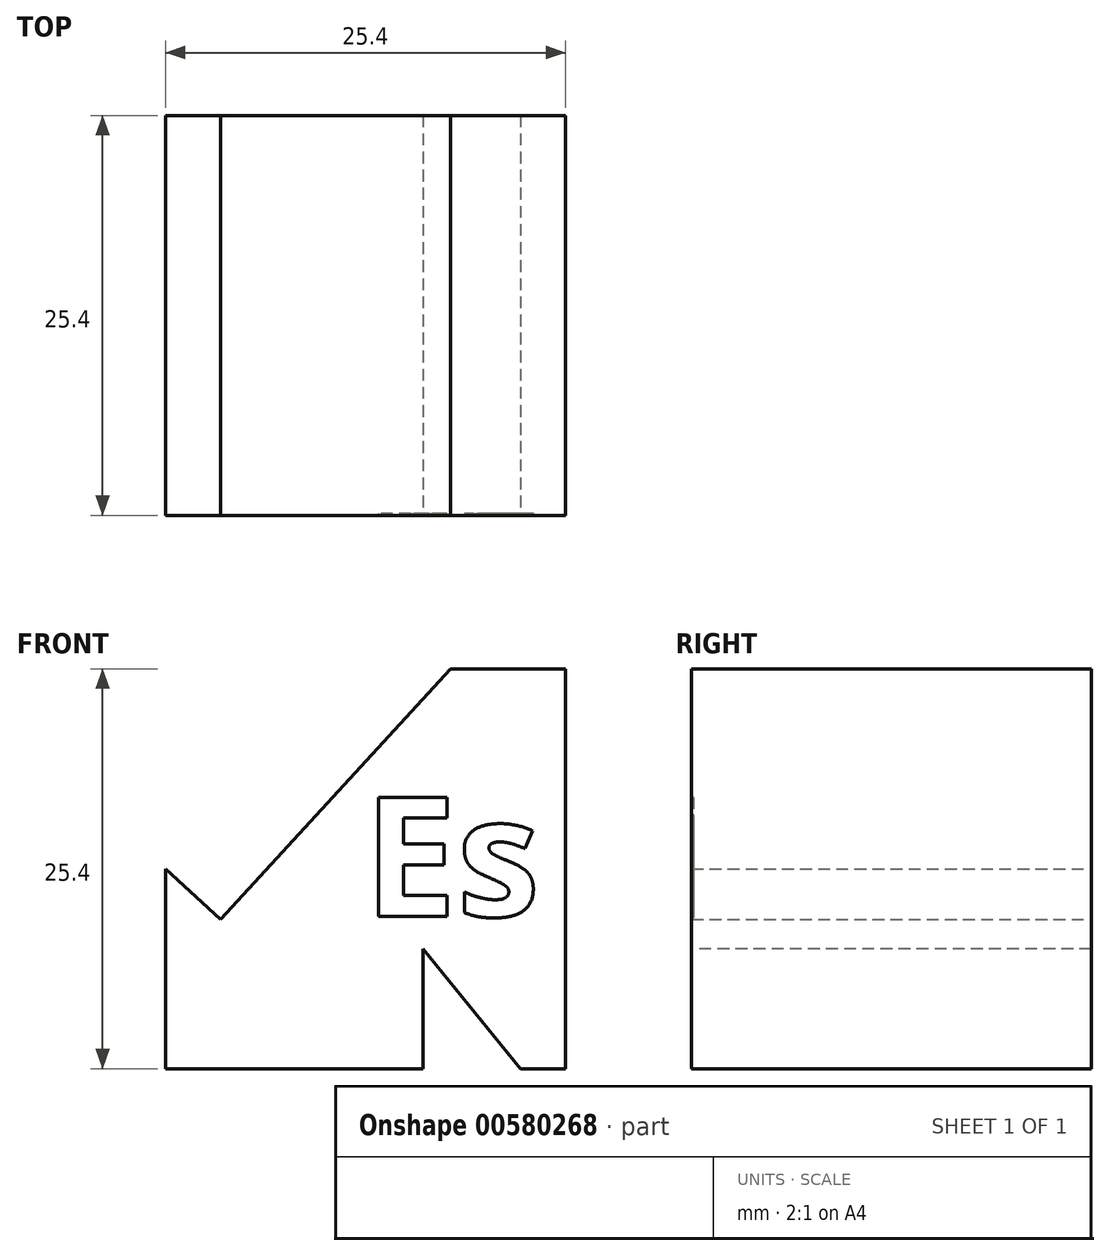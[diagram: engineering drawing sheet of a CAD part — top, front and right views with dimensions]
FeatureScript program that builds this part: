
annotation { "Feature Type Name" : "Feature", "Feature Type Description" : "" }
export const myFeature = defineFeature(function(context is Context, id is Id, definition is map)
    precondition{}
    {
        {
            var Q0;
            Q0=qCreatedBy(makeId("Front.planeOp"),FACE);
            var sketch = newSketch(context, id + "F0", { "sketchPlane" : qUnion([Q0])});
            skLineSegment(sketch, "E0.bottom", {"start": v(-12.7, 12.7) * mm, "end": v(12.7, 12.7) * mm});
            skLineSegment(sketch, "E0.top", {"start": v(-12.7, -12.7) * mm, "end": v(12.7, -12.7) * mm});
            skLineSegment(sketch, "E0.left", {"start": v(-12.7, 12.7) * mm, "end": v(-12.7, -12.7) * mm});
            skLineSegment(sketch, "E0.right", {"start": v(12.7, 12.7) * mm, "end": v(12.7, -12.7) * mm});
            skPoint(sketch, "E0.middle", {"position": v(0, 0) * mm});
            skSolve(sketch);
        }
        {
            var Q0;
            Q0=makeQuery(id+"F0.imprint","IMPRINT",FACE,{"disambiguationData":[TD([[makeQuery(id+"F0.imprint","IMPRINT",EDGE,{"derivedFrom":sQuery(id+"F0.wireOp",EDGE,"E0.bottom")}),-1.0]])]});
            extrude(context, id + "F1", {"entities" : qUnion([Q0]), "depth" : 25.4 * mm, "offsetDistance" : 25.4 * mm});
        }
        {
            var Q0;
            Q0=makeQuery(id+"F1.opExtrude","CAP_FACE",FACE,{"disambiguationData":[OSD([sQuery(id+"F0.wireOp",EDGE,"E0.bottom"),sQuery(id+"F0.wireOp",EDGE,"E0.top"),sQuery(id+"F0.wireOp",EDGE,"E0.left"),sQuery(id+"F0.wireOp",EDGE,"E0.right")])],"isStart":false});
            var sketch = newSketch(context, id + "F2", { "sketchPlane" : qUnion([Q0])});
            skLineSegment(sketch, "E1", {"start": v(3.66, -12.7) * mm, "end": v(3.66, -5.08) * mm});
            skLineSegment(sketch, "E2", {"start": v(3.66, -5.08) * mm, "end": v(9.83, -12.7) * mm});
            skLineSegment(sketch, "E3", {"start": v(9.83, -12.7) * mm, "end": v(3.66, -12.7) * mm});
            skSolve(sketch);
        }
        {
            var Q0;
            Q0=makeQuery(id+"F2.imprint","IMPRINT",FACE,{"disambiguationData":[TD([[makeQuery(id+"F2.imprint","IMPRINT",EDGE,{"derivedFrom":sQuery(id+"F2.wireOp",EDGE,"E1")}),-1.0]])]});
            extrude(context, id + "F3", {"entities" : qUnion([Q0]), "operationType" : NewBodyOperationType.REMOVE, "endBound" : BoundingType.THROUGH_ALL, "oppositeDirection" : true, "depth" : 25.4 * mm, "offsetDistance" : 25.4 * mm});
        }
        {
            var Q0;
            Q0=makeQuery(id+"F1.opExtrude","CAP_FACE",FACE,{"disambiguationData":[OSD([sQuery(id+"F0.wireOp",EDGE,"E0.bottom"),sQuery(id+"F0.wireOp",EDGE,"E0.top"),sQuery(id+"F0.wireOp",EDGE,"E0.left"),sQuery(id+"F0.wireOp",EDGE,"E0.right")])],"isStart":false});
            var sketch = newSketch(context, id + "F4", { "sketchPlane" : qUnion([Q0])});
            skLineSegment(sketch, "E4", {"start": v(5.4, 12.7) * mm, "end": v(-12.7, -7.01) * mm});
            skLineSegment(sketch, "E5", {"start": v(-12.7, -7.01) * mm, "end": v(-12.7, 12.7) * mm});
            skLineSegment(sketch, "E6", {"start": v(-12.7, 12.7) * mm, "end": v(5.4, 12.7) * mm});
            skSolve(sketch);
        }
        {
            var Q0;
            Q0=makeQuery(id+"F4.imprint","IMPRINT",FACE,{"disambiguationData":[TD([[makeQuery(id+"F4.imprint","IMPRINT",EDGE,{"derivedFrom":sQuery(id+"F4.wireOp",EDGE,"E4")}),-1.0]])]});
            extrude(context, id + "F5", {"entities" : qUnion([Q0]), "operationType" : NewBodyOperationType.REMOVE, "endBound" : BoundingType.THROUGH_ALL, "oppositeDirection" : true, "depth" : 25.4 * mm, "offsetDistance" : 25.4 * mm});
        }
        {
            var Q0;
            Q0=makeQuery(id+"F1.opExtrude","CAP_FACE",FACE,{"disambiguationData":[OSD([sQuery(id+"F0.wireOp",EDGE,"E0.bottom"),sQuery(id+"F0.wireOp",EDGE,"E0.top"),sQuery(id+"F0.wireOp",EDGE,"E0.left"),sQuery(id+"F0.wireOp",EDGE,"E0.right")])],"isStart":true});
            var sketch = newSketch(context, id + "F6", { "sketchPlane" : qUnion([Q0])});
            skLineSegment(sketch, "E7", {"start": v(12.7, -7.01) * mm, "end": v(12.7, 0) * mm});
            skLineSegment(sketch, "E8", {"start": v(12.7, 0) * mm, "end": v(8.88, -3.5) * mm});
            skPoint(sketch, "E8.endSnap0", {"position": v(12.7, -3.5) * mm});
            skSolve(sketch);
        }
        {
            var Q0;
            Q0=makeQuery(id+"F1.opExtrude","CAP_FACE",FACE,{"disambiguationData":[OSD([sQuery(id+"F0.wireOp",EDGE,"E0.bottom"),sQuery(id+"F0.wireOp",EDGE,"E0.top"),sQuery(id+"F0.wireOp",EDGE,"E0.left"),sQuery(id+"F0.wireOp",EDGE,"E0.right")])],"isStart":false});
            var sketch = newSketch(context, id + "F7", { "sketchPlane" : qUnion([Q0])});
            skSolve(sketch);
        }
        {
            var Q0;
            {var subQ0=sQuery(id+"F6.wireOp",EDGE,"E7");Q0=makeQuery(id+"F6.imprint","IMPRINT",FACE,{"disambiguationData":[TD([[makeQuery(id+"F6.imprint","IMPRINT",EDGE,{"derivedFrom":subQ0}),1.0]])]});}
            var Q1;
            {var subQ0=sQuery(id+"F7.wireOp",EDGE,"KE9NxnWJ-8wBy-2ygz-UcdU-bdd0KeWZWIvf");Q1=makeQuery(id+"F7.imprint","IMPRINT",FACE,{"disambiguationData":[TD([[makeQuery(id+"F7.imprint","IMPRINT",EDGE,{"derivedFrom":subQ0}),-1.0]])]});}
            extrude(context, id + "F8", {"entities" : qUnion([Q0, Q1]), "operationType" : NewBodyOperationType.ADD, "oppositeDirection" : true, "depth" : 25.4 * mm, "offsetDistance" : 25.4 * mm});
        }
        {
            var Q0;
            {var subQ0=sQuery(id+"F0.wireOp",EDGE,"E0.right");Q0=makeQuery(id+"F7.imprint","IMPRINT",FACE,{"disambiguationData":[TD([[makeQuery(id+"F7.imprint","IMPRINT",EDGE,{"derivedFrom":makeQuery(id+"F1.opExtrude","CAP_EDGE",EDGE,{"disambiguationData":[OSD([subQ0])],"isStart":false})}),-1.0]])]});}
            var sketch = newSketch(context, id + "F9", { "sketchPlane" : qUnion([Q0])});
            skText(sketch, "E9", { "text": "Es", "fontName": "OpenSans-Bold.ttf"});
            const initialGuessF9  = {"E9": [-0.00013, -0.00302, 1, 0, 0.00762]};
            skSetInitialGuess(sketch, initialGuessF9);
            skSolve(sketch);
        }
        {
            var Q0;
            Q0 = qSketchRegion(id + "F9", true);
            extrude(context, id + "F10", {"entities" : qUnion([Q0]), "operationType" : NewBodyOperationType.REMOVE, "endBound" : BoundingType.SYMMETRIC, "oppositeDirection" : true, "depth" : 0.25 * mm, "offsetDistance" : 25.4 * mm});
        }
    });
